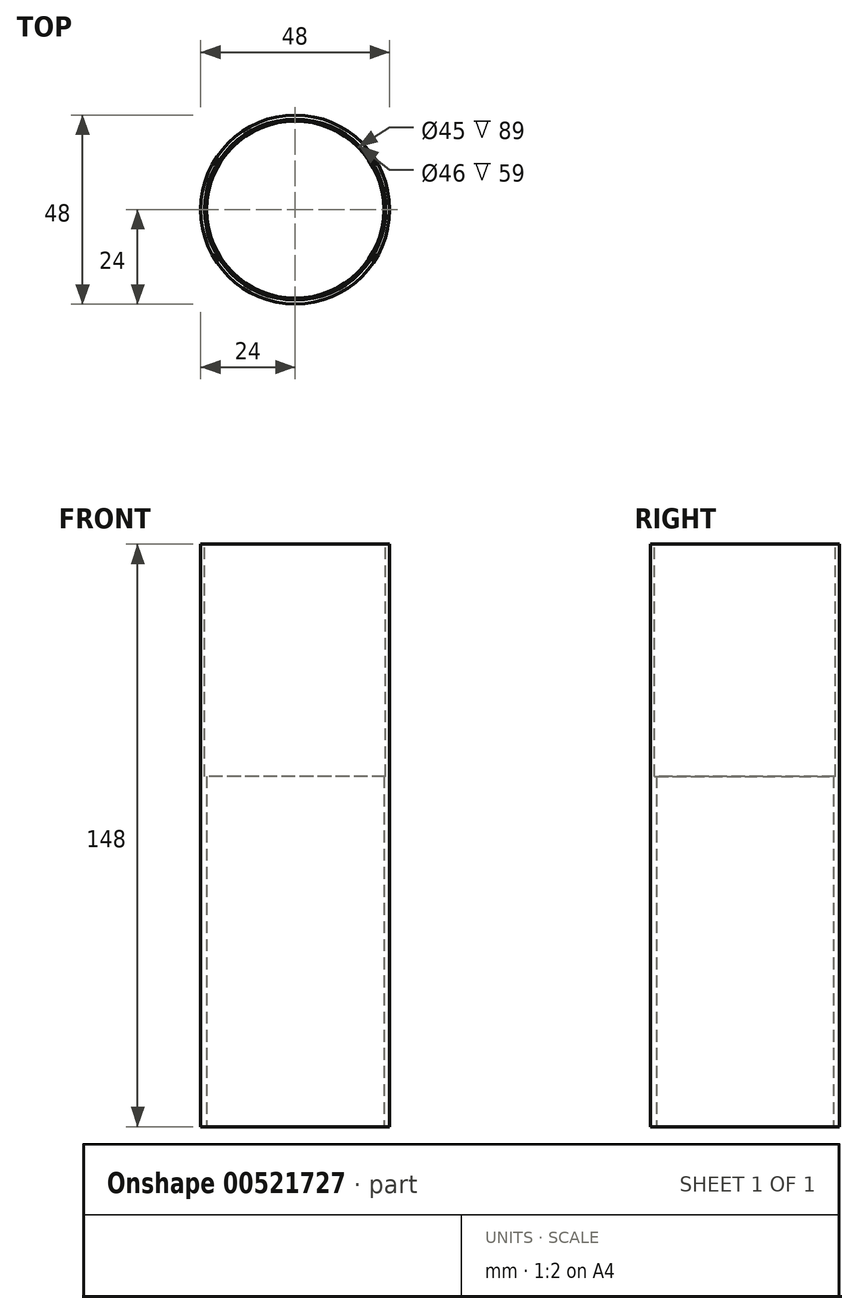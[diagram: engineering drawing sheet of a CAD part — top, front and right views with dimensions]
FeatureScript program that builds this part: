
annotation { "Feature Type Name" : "Feature", "Feature Type Description" : "" }
export const myFeature = defineFeature(function(context is Context, id is Id, definition is map)
    precondition{}
    {
        {
            var Q0;
            Q0=qCreatedBy(makeId("Top.planeOp"),FACE);
            var sketch = newSketch(context, id + "F0", { "sketchPlane" : qUnion([Q0])});
            skCircle(sketch, "E0", {"center": v(0, 0) * mm, "radius": 24 * mm});
            skCircle(sketch, "E1", {"center": v(0, 0) * mm, "radius": 22.5 * mm});
            skSolve(sketch);
        }
        {
            var Q0;
            Q0 = qSketchRegion(id + "F0", true);
            extrude(context, id + "F1", {"entities" : qUnion([Q0]), "depth" : 148 * mm, "offsetDistance" : 25.4 * mm});
        }
        {
            var Q0;
            Q0=makeQuery(id+"F1.opExtrude","CAP_FACE",FACE,{"disambiguationData":[OSD([sQuery(id+"F0.wireOp",EDGE,"E0"),sQuery(id+"F0.wireOp",EDGE,"E1")])],"isStart":false});
            var sketch = newSketch(context, id + "F2", { "sketchPlane" : qUnion([Q0])});
            skCircle(sketch, "E2", {"center": v(0, 0) * mm, "radius": 23 * mm});
            skSolve(sketch);
        }
        {
            var Q0;
            Q0 = qSketchRegion(id + "F2", true);
            extrude(context, id + "F3", {"entities" : qUnion([Q0]), "operationType" : NewBodyOperationType.REMOVE, "oppositeDirection" : true, "depth" : 59 * mm, "offsetDistance" : 25.4 * mm});
        }
    });
